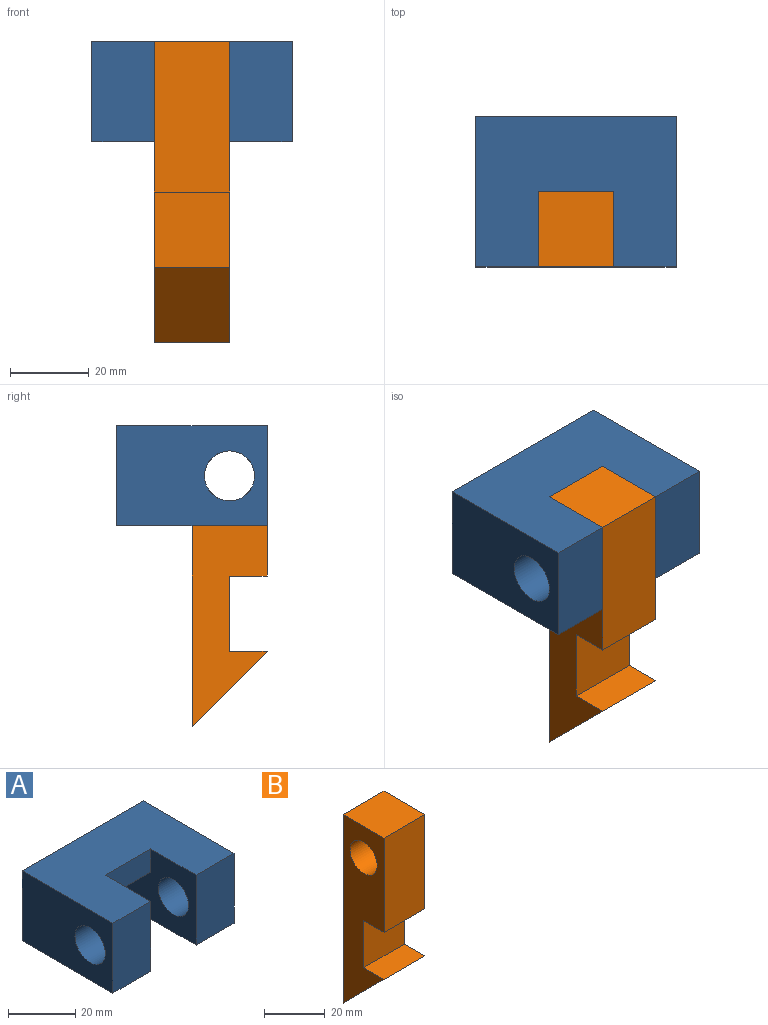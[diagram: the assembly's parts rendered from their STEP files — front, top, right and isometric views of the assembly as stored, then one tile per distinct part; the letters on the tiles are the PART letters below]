
ASSEMBLY  parts=2 mates=1
PART A: 14 faces, bbox 50.8x38.1x25.4 mm
  f0: plane 38.1x15.88mm, normal (0,0,-1), area 604.8mm2, adj f6,f8,f10,f11
  f1: plane 19.05x8.43mm, normal (0,-1,0), area 160.6mm2, adj f5,f11,f12,f13
  f2: plane 25.4x15.88mm, normal (0,-1,0), area 403.2mm2, adj f3,f5,f9,f12
  f3: plane 38.1x15.88mm, normal (0,0,-1), area 604.8mm2, adj f2,f8,f9,f12
  f4: cylinder r=6.35mm len=15.88mm, axis (-1,0,0), area 633.4mm2, adj f9,f12
  f5: plane 50.8x38.1mm, normal (0,0,1), area 1572.6mm2, adj f1,f2,f6,f8,f9,f10,f11,f12
  f6: plane 25.4x15.88mm, normal (0,-1,0), area 403.2mm2, adj f0,f5,f10,f11
  f7: cylinder r=6.35mm len=15.88mm, axis (-1,0,0), area 633.4mm2, adj f10,f11
  f8: plane 50.8x25.4mm, normal (0,1,0), area 1290.3mm2, adj f0,f3,f5,f9,f10,f13
  f9: plane 38.1x25.4mm, normal (1,0,0), area 841.1mm2, adj f2,f3,f4,f5,f8
  f10: plane 38.1x25.4mm, normal (-1,0,0), area 841.1mm2, adj f0,f5,f6,f7,f8
  f11: plane 38.1x25.4mm, normal (1,0,0), area 518.8mm2, adj f0,f1,f5,f6,f7,f13
  f12: plane 38.1x25.4mm, normal (-1,0,0), area 518.8mm2, adj f1,f2,f3,f4,f5,f13
  f13: plane 19.05x19.05mm, normal (0,-0.67,-0.75), area 486mm2, adj f1,f8,f11,f12
PART B: 10 faces, bbox 19.1x19.1x76.2 mm
  f0: plane 19.05x19.05mm, normal (0,-1,0), area 362.9mm2, adj f1,f7,f8,f9
  f1: plane 19.05x9.53mm, normal (0,0,1), area 181.5mm2, adj f0,f2,f8,f9
  f2: plane 19.05x19.05mm, normal (0,-0.71,-0.71), area 513.2mm2, adj f1,f3,f8,f9
  f3: plane 76.2x19.05mm, normal (0,1,0), area 1451.6mm2, adj f2,f4,f8,f9
  f4: plane 19.05x19.05mm, normal (0,0,1), area 362.9mm2, adj f3,f5,f8,f9
  f5: plane 38.1x19.05mm, normal (0,-1,0), area 725.8mm2, adj f4,f7,f8,f9
  f6: cylinder r=6.35mm len=19.05mm, axis (-1,0,0), area 760.1mm2, adj f8,f9
  f7: plane 19.05x9.53mm, normal (0,0,-1), area 181.5mm2, adj f0,f5,f8,f9
  f8: plane 76.2x19.05mm, normal (1,0,0), area 962mm2, adj f0,f1,f2,f3,f4,f5,f6,f7
  f9: plane 76.2x19.05mm, normal (-1,0,0), area 962mm2, adj f0,f1,f2,f3,f4,f5,f6,f7
PLACE A t=(-6.51,14.11,35.77)mm fixed
PLACE B t=(-6.51,14.11,35.77)mm
MATE revolute B.f6 <-> A.f4  axis (1,0,0) through (3.01,14.11,61.17)mm
